MODEL slx_3bda52900c58
CONFIG AbsTol = auto
CONFIG EnableMultiTasking = off
CONFIG FixedStep = auto
CONFIG MaxStep = auto
CONFIG MinStep = auto
CONFIG RelTol = 1e-3
CONFIG SampleTimeConstraint = Unconstrained
CONFIG SolverName = VariableStepAuto
CONFIG StartTime = 0.0
CONFIG StopTime = 10.0
BLOCK [BusSelector] Bus Selector
  OutputSignals = Electrical torque Te (n m),Speed wm (rad/s)
BLOCK [Constant] Constant
  NameLocation = top
  Value = 0.5
BLOCK [Reference] Current Measurement  REF=spsCurrentMeasurementLib/Current Measurement
  LibrarySourceBlock = sps_lib/Sensors and Measurements/Current Measurement
  SourceBlock = spsCurrentMeasurementLib/Current Measurement
  SourceType = Current Measurement
  UserDataPersistent = on
BLOCK [Reference] DC Machine  REF=spsDCMachineLib/DC Machine
  LibrarySourceBlock = sps_lib/Electrical Machines/DC Machine
  SourceBlock = spsDCMachineLib/DC Machine
  SourceType = DC machine
BLOCK [Reference] DC Voltage Source  REF=spsDCVoltageSourceLib/DC Voltage Source
  LibrarySourceBlock = sps_lib/Sources/DC Voltage Source
  SourceBlock = spsDCVoltageSourceLib/DC Voltage Source
  SourceType = DC Voltage Source
BLOCK [Reference] DC Voltage Source1  REF=spsDCVoltageSourceLib/DC Voltage Source
  LibrarySourceBlock = sps_lib/Sources/DC Voltage Source
  SourceBlock = spsDCVoltageSourceLib/DC Voltage Source
  SourceType = DC Voltage Source
BLOCK [Reference] Ground  REF=spsGroundLib/Ground
  LibrarySourceBlock = sps_lib/Utilities/Ground
  NameLocation = right
  SourceBlock = spsGroundLib/Ground
  SourceType = Ground
BLOCK [Reference] Mosfet  REF=spsMosfetLib/Mosfet
  LibrarySourceBlock = sps_lib/Power Electronics/Mosfet
  NameLocation = left
  SourceBlock = spsMosfetLib/Mosfet
  SourceType = Mosfet
BLOCK [Reference] Mosfet1  REF=spsMosfetLib/Mosfet
  LibrarySourceBlock = sps_lib/Power Electronics/Mosfet
  NameLocation = left
  SourceBlock = spsMosfetLib/Mosfet
  SourceType = Mosfet
BLOCK [Logic] NOT
  AllPortsSameDT = off
  IconShape = distinctive
  NameLocation = top
  Operator = NOT
  OutDataTypeStr = boolean
BLOCK [Reference] PWM Generator  REF=eePwmGenerator/PWM Generator
  LibrarySourceBlock = ee_sl_lib/Pulse Width
Modulation/PWM Generator
  NameLocation = top
  SourceBlock = eePwmGenerator/PWM Generator
  SourceType = PWM Generator
BLOCK [Reference] Ramp  REF=simulink/Sources/Ramp
  NameLocation = left
  SourceBlock = simulink/Sources/Ramp
  SourceType = Ramp
BLOCK [Scope] Scope1
  ActiveDisplayYMaximum = 108.5704695468584
  ActiveDisplayYMinimum = -98.931141586337333
  DataLoggingVariableName = ScopeData1
  Floating = off
  GraphicalSettings = {"AxesScalingProperties":{"AlignXAxis":"Center","AlignYAxis":"Center","AutoScaleXAxisLimits":false,"AxesScaling":"Manual","AxesScalingNumUpdates":10,"ExpandOnly":true,"ScaleAxesLimitsAtStop":false,"XAxisDataRange":100,"YAxisDataRange":80},"DisplayProperties":{"ColorOrder":["auto","auto","auto","auto","auto","auto","auto","auto","auto","auto","auto","auto","auto","auto","auto","auto","auto","auto",...<+2169ch>
  MultipleDisplayCache = [{"MaxYLimMag":243.13609469540555,"MaxYLimReal":108.5704695468584,"MinYLimMag":0,"MinYLimReal":-98.931141586337333,"PlotAsMagnitudePhase":false,"ShowGrid":true,"ShowLegend":true,"Title":"%<SignalLabel>","YLabel":""}]
  NumInputPorts = 2
  ScopeFrameLocation = window
  ShowLegend = on
  WasSavedAsWebScope = on
  WindowPosition = [1.000000,41.000000,1536.000000,801.000000,]
BLOCK [Scope] Scope2
  ActiveDisplayYMaximum = 214.61794168829476
  ActiveDisplayYMinimum = -23.897668085148219
  DataLoggingVariableName = ScopeData2
  Floating = off
  GraphicalSettings = {"Style":{"BackgroundColor":[0.12941176470588237,0.12941176470588237,0.12941176470588237],"AxesColor":[0.07058823529411765,0.07058823529411765,0.07058823529411765],"LabelsColor":[0.8509803921568627,0.8509803921568627,0.8509803921568627],"PreserveColors":false,"Visible":[true],"LineStyle":["-"],"LineWidth":[1.5],"BarWidth":[0.9],"LineColor":["auto"],"LineFaceAlpha":[1],"LineEdgeAlpha":[1],"Marker":...<+1944ch>
  MultipleDisplayCache = [{"MaxYLimMag":214.61794168829476,"MaxYLimReal":214.61794168829476,"MinYLimMag":0,"MinYLimReal":-23.897668085148219,"PlotAsMagnitudePhase":false,"ShowGrid":true,"ShowLegend":false,"Title":"%<SignalLabel>","YLabel":""}]
  NumInputPorts = 1
  ScopeFrameLocation = window
  WasSavedAsWebScope = on
  WindowPosition = [1.000000,41.000000,1536.000000,801.000000,]
BLOCK [Scope] Scope3
  ActiveDisplayYMaximum = 163.02404537020993
  ActiveDisplayYMinimum = -18.112005069578423
  DataLoggingVariableName = ScopeData3
  Floating = off
  GraphicalSettings = {"AxesScalingProperties":{"AlignXAxis":"Center","AlignYAxis":"Center","AutoScaleXAxisLimits":false,"AxesScaling":"Manual","AxesScalingNumUpdates":10,"ExpandOnly":true,"ScaleAxesLimitsAtStop":false,"XAxisDataRange":100,"YAxisDataRange":80},"DisplayProperties":{"ColorOrder":["auto","auto","auto","auto","auto","auto","auto","auto","auto","auto","auto","auto","auto","auto","auto","auto","auto","auto",...<+1936ch>
  MultipleDisplayCache = [{"MaxYLimMag":163.02404537020993,"MaxYLimReal":163.02404537020993,"MinYLimMag":0,"MinYLimReal":-18.112005069578423,"PlotAsMagnitudePhase":false,"ShowGrid":true,"ShowLegend":false,"Title":"%<SignalLabel>","YLabel":""}]
  NumInputPorts = 1
  ScopeFrameLocation = window
  WasSavedAsWebScope = on
  WindowPosition = [1.000000,41.000000,1536.000000,801.000000,]
BLOCK [Scope] Scope4
  ActiveDisplayYMaximum = 1.125
  ActiveDisplayYMinimum = -0.12499999999999997
  Floating = off
  GraphicalSettings = {"Style":{"BackgroundColor":[0.12941176470588237,0.12941176470588237,0.12941176470588237],"AxesColor":[0.07058823529411765,0.07058823529411765,0.07058823529411765],"LabelsColor":[0.8509803921568627,0.8509803921568627,0.8509803921568627],"PreserveColors":false,"Visible":[true,true],"LineStyle":["-","-"],"LineWidth":[1.5,1.5],"BarWidth":[0.9,0.9],"LineColor":["auto","auto"],"LineFaceAlpha":[1,1],"Li...<+2068ch>
  MultipleDisplayCache = [{"MaxYLimMag":1.125,"MaxYLimReal":1.125,"MinYLimMag":0,"MinYLimReal":-0.12499999999999997,"PlotAsMagnitudePhase":false,"ShowGrid":true,"ShowLegend":true,"Title":"%<SignalLabel>","YLabel":""}]
  NameLocation = top
  NumInputPorts = 2
  ScopeFrameLocation = window
  ShowLegend = on
  WasSavedAsWebScope = on
  WindowPosition = [1.000000,41.000000,1536.000000,801.000000,]
BLOCK [Scope] Scope5
  ActiveDisplayYMaximum = 59.527431820714391
  ActiveDisplayYMinimum = -5.503063409763616
  DataLoggingVariableName = ScopeData4
  Floating = off
  GraphicalSettings = {"Style":{"BackgroundColor":[0.12941176470588237,0.12941176470588237,0.12941176470588237],"AxesColor":[0.07058823529411765,0.07058823529411765,0.07058823529411765],"LabelsColor":[0.8509803921568627,0.8509803921568627,0.8509803921568627],"PreserveColors":false,"Visible":[true],"LineStyle":["-"],"LineWidth":[1.5],"BarWidth":[0.9],"LineColor":["auto"],"LineFaceAlpha":[1],"LineEdgeAlpha":[1],"Marker":...<+1924ch>
  MultipleDisplayCache = [{"MaxYLimMag":59.527431820714391,"MaxYLimReal":59.527431820714391,"MinYLimMag":0,"MinYLimReal":-5.503063409763616,"PlotAsMagnitudePhase":false,"ShowGrid":true,"ShowLegend":false,"Title":"%<SignalLabel>","YLabel":""}]
  NumInputPorts = 1
  ScopeFrameLocation = window
  WasSavedAsWebScope = on
  WindowPosition = [1.000000,41.000000,1536.000000,801.000000,]
BLOCK [Reference] Series RLC Branch  REF=spsSeriesRLCBranchLib/Series RLC Branch
  LibrarySourceBlock = sps_lib/Passives/Series RLC Branch
  SourceBlock = spsSeriesRLCBranchLib/Series RLC Branch
  SourceType = Series RLC Branch
BLOCK [Reference] Series RLC Branch1  REF=spsSeriesRLCBranchLib/Series RLC Branch
  LibrarySourceBlock = sps_lib/Passives/Series RLC Branch
  NameLocation = left
  SourceBlock = spsSeriesRLCBranchLib/Series RLC Branch
  SourceType = Series RLC Branch
BLOCK [Reference] Voltage Measurement  REF=spsVoltageMeasurementLib/Voltage Measurement
  LibrarySourceBlock = sps_lib/Sensors and Measurements/Voltage Measurement
  SourceBlock = spsVoltageMeasurementLib/Voltage Measurement
  SourceType = Voltage Measurement
  UserDataPersistent = on
BLOCK [Reference] Voltage Measurement1  REF=spsVoltageMeasurementLib/Voltage Measurement
  LibrarySourceBlock = sps_lib/Sensors and Measurements/Voltage Measurement
  NameLocation = left
  SourceBlock = spsVoltageMeasurementLib/Voltage Measurement
  SourceType = Voltage Measurement
  UserDataPersistent = on
BLOCK [Reference] powergui  REF=sps_lib/powergui
  LibrarySourceBlock = sps_lib/powergui
  Priority = 1
  SourceBlock = sps_lib/powergui
  SourceType = PSB option menu block
LINE Bus Selector:1 -> Scope2:1
LINE Bus Selector:2 -> Scope5:1
LINE Constant:1 -> PWM Generator:1
LINE Current Measurement:1 -> Scope1:1
LINE Current Measurement:rconn -> Series RLC Branch1:lconn
LINE DC Machine:1 -> Bus Selector:1
LINE DC Voltage Source1:lconn -> DC Machine:rconn
LINE DC Voltage Source1:rconn -> DC Machine:lconn
LINE DC Voltage Source:lconn -> Mosfet1:rconn
LINE DC Voltage Source:rconn -> Mosfet:lconn
LINE Mosfet:rconn -> Mosfet1:lconn
LINE NOT:1 -> Mosfet1:1
LINE NOT:1 -> Scope4:2
LINE PWM Generator:1 -> Mosfet:1
LINE PWM Generator:1 -> NOT:1
LINE PWM Generator:1 -> Scope4:1
LINE Ramp:1 -> DC Machine:1
LINE Series RLC Branch:rconn -> Current Measurement:lconn
LINE Voltage Measurement1:1 -> Scope3:1
LINE Voltage Measurement:1 -> Scope1:2
